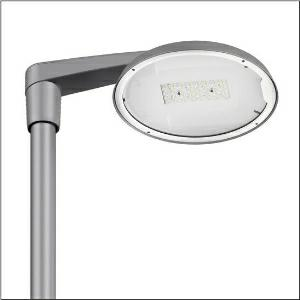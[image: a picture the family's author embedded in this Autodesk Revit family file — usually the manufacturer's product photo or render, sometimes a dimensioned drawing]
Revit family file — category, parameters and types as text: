
# Revit family: dl_50_iq_mini___st0_5a_5xa248b31f08he_1b70
name_source: partatom
category: Lighting Fixtures
units: mm (PartAtom-declared; Revit-internal decimal feet)

## family parameters
Cut with Voids When Loaded = No
Host = Face
Light Source = No
Part Type = Normal
Room Calculation Point = No
Round Connector Dimension = Use Diameter
Shared = No

## types (1)
- --- (1 x LED, 9400 lm, 68.6 W, 3000K)
    Apparent Load = 69 VA
    CIE Flux Codes = 41 75 97 100 100
    Color Rendering = 70
    Color Temperature = 3000K
    Default Elevation = 1800 mm
    Description = DL 50 iQ mini, mast luminaire, primary light control with lens, of PMMA, primary optical cover: cover, of toughened safety glass, transparent, light distribution: ST0.5a, light emission: direct distribution, primary light characteristic: asymmetric, installation type: side-entry, post-top, LED, High Power LED, rated luminous flux: 9.400lm, luminous efficacy: 137lm/W, light colour: 730, colour temperature: 3000K, control gear: iQ Street-Remote, control: optimised constant luminous flux control (CLO 2.0), Desk-Remote (wireless, voltage-free reading and setting of iQ features in the workshop via application-optimized NFC function/RFID function), Light-Fading, Smart-Wire, Night-Set, Lumen-Switch, Temp-Guard, Auto-Match, Street-Remote, mains connection: 230..240V, AC, 50/60Hz, connection cable pre-assembled, cable length: 8,5m, start of lifetime: 69W, end of service life: 72W, reduction: 30W, luminaire housing, of diecast aluminium, powder-coated, SITECO metallic grey (DB 702S), inclination adjustable: 0°, 5°, 10° (post-top) | 0°, -5°, -10°, -15° (side-entry), please order mast post-top element or mast side-entry element separately, diameter: 500mm, height: 115mm, post-top: for spigot size d x l = 76 x 100mm; with reducer (optional accessory) 60 x 100mm | side-entry: for spigot size d x l = 60 x 100mm; with reducer (optional accessory) 42 x 100mm, mounting height: 4..6m, protection rating (complete): IP66, insulation class (complete): insulation class II (safety insulation), certification: CE, ENEC, ENEC+, VDE, impact resistance: IK08, permissible operating ambient temperature for outdoor applications: -25..+40°C, standard-compliant lighting for roads and squares, packaging unit: 1 piece

Light Distribution: ST0.5a
    Height = 115 mm
    Lamp = 1 x LED
    Lamp Light Flux = 9400 lm
    Lamp Power = 68.6 W
    Lamp count = 1
    Length = 500 mm
    Luminous efficacy = 137 lm/W
    Manufacturer = Siteco
    ModVariant = No
    Model = 5XA248B31F08HE
    Number of Poles = 1
    OnlyDefault = Yes
    Power Factor = 1
    Product Name = DL 50 iQ mini | ST0.5a
    Product group = mast luminaire | pylon top
    ProductGroupID = 6100
    Protection Class = Protection class II
    Protection Degree = IP 66
    RLX_Detail_Level = 1
    RLX_Emergency_Light_Flux = 0 lm
    RLX_Emergency_Type = 0
    RLX_Emergency_Type_DB = No
    RlxData = <blob elided: 126581 chars, md5=6a360886>
    Socket = socket
    Standby Power = 0 W
    System Light Flux = 9400 lm
    System Power = 69 W
    Type Comments = factory setting: luminous flux: 100 % | dim-lin: 254 | 693 mA
    Type Image = l_1251794.jpg
    URL = http://relux.com
    VarID = @adj_142719
    Voltage = 0 V
    Weight = 0.00 kg
    Width = 0 mm  [stored 0 ft]

note: [stored X ft] marks values corroborated as IEEE doubles in the binary element streams (Revit-internal decimal feet)

## geometry (parser evidence)
native form markers: Blend x4, Sweep x10
no freeform markers — native parametric forms only
